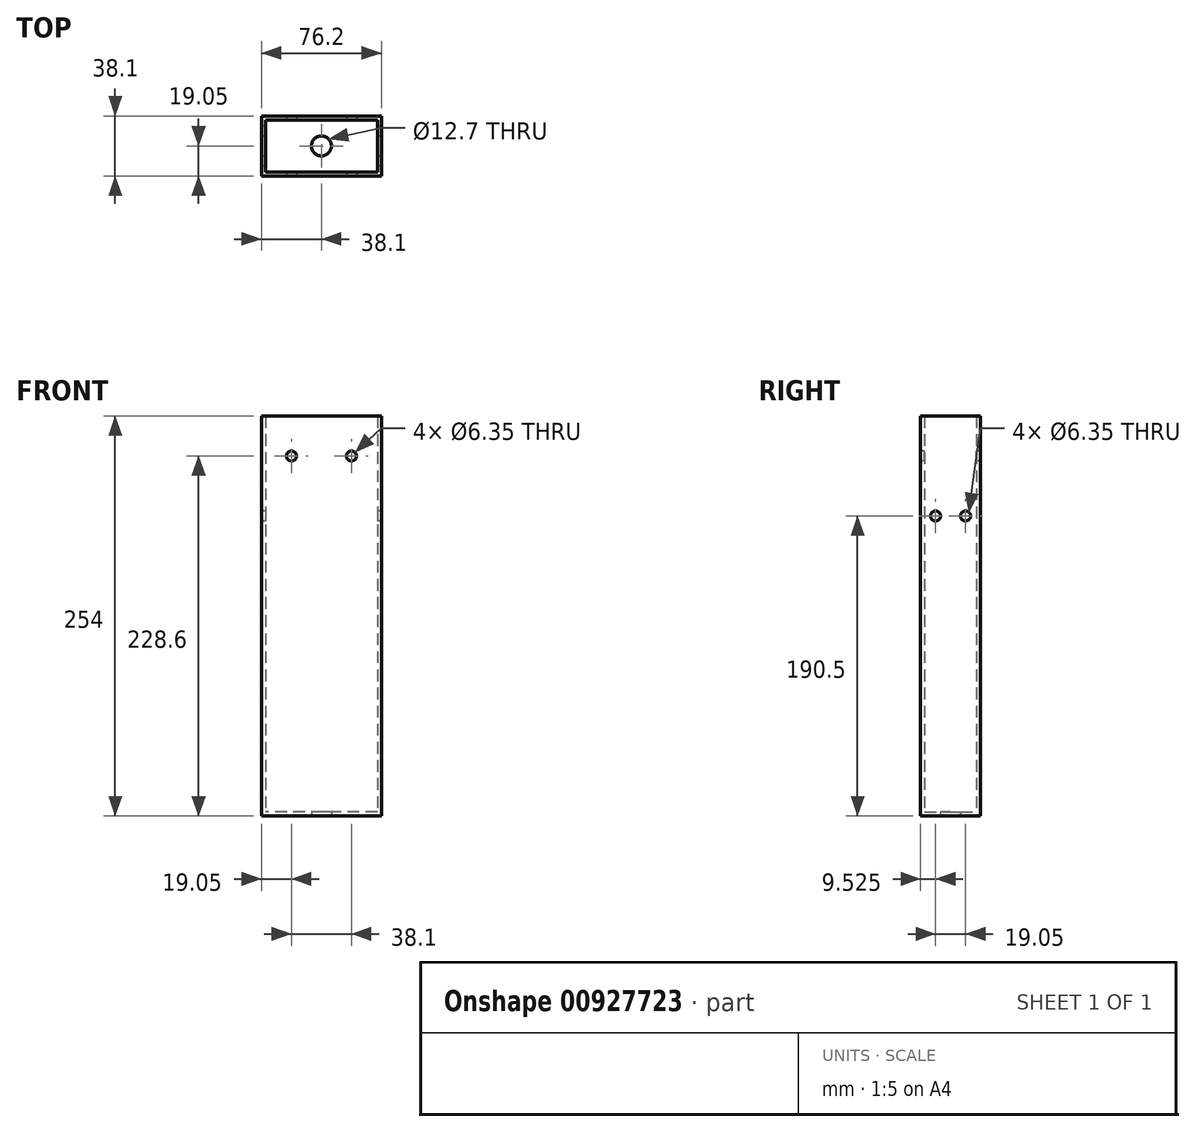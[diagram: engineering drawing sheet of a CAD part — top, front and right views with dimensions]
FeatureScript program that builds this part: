
annotation { "Feature Type Name" : "Feature", "Feature Type Description" : "" }
export const myFeature = defineFeature(function(context is Context, id is Id, definition is map)
    precondition{}
    {
        {
            var Q0;
            Q0=qCreatedBy(makeId("Top.planeOp"),FACE);
            var sketch = newSketch(context, id + "F0", { "sketchPlane" : qUnion([Q0])});
            skLineSegment(sketch, "E0.bottom", {"start": v(38.1, -19.05) * mm, "end": v(-38.1, -19.05) * mm});
            skLineSegment(sketch, "E0.top", {"start": v(38.1, 19.05) * mm, "end": v(-38.1, 19.05) * mm});
            skLineSegment(sketch, "E0.left", {"start": v(38.1, -19.05) * mm, "end": v(38.1, 19.05) * mm});
            skLineSegment(sketch, "E0.right", {"start": v(-38.1, -19.05) * mm, "end": v(-38.1, 19.05) * mm});
            skPoint(sketch, "E0.middle", {"position": v(0, 0) * mm});
            skSolve(sketch);
        }
        {
            var Q0;
            Q0=makeQuery(id+"F0.imprint","IMPRINT",FACE,{"disambiguationData":[TD([[makeQuery(id+"F0.imprint","IMPRINT",EDGE,{"derivedFrom":sQuery(id+"F0.wireOp",EDGE,"E0.bottom")}),-1.0]])]});
            extrude(context, id + "F1", {"entities" : qUnion([Q0]), "depth" : 254 * mm, "offsetDistance" : 25.4 * mm});
        }
        {
            var Q0;
            Q0=makeQuery(id+"F1.opExtrude","CAP_FACE",FACE,{"disambiguationData":[OSD([sQuery(id+"F0.wireOp",EDGE,"E0.bottom"),sQuery(id+"F0.wireOp",EDGE,"E0.top"),sQuery(id+"F0.wireOp",EDGE,"E0.left"),sQuery(id+"F0.wireOp",EDGE,"E0.right")])],"isStart":false});
            shell(context, id + "F2", {"entities" : qUnion([Q0]), "thickness" : 2.54 * mm});
        }
        {
            var Q0;
            Q0=makeQuery(id+"F1.opExtrude","SWEPT_FACE",FACE,{"disambiguationData":[OSD([sQuery(id+"F0.wireOp",EDGE,"E0.right")])]});
            var sketch = newSketch(context, id + "F3", { "sketchPlane" : qUnion([Q0])});
            skPoint(sketch, "E1", {"position": v(-9.52, 190.5) * mm});
            skPoint(sketch, "E2", {"position": v(9.53, 190.5) * mm});
            skSolve(sketch);
        }
        {
            var Q0;
            Q0=makeQuery(id+"F1.opExtrude","SWEPT_FACE",FACE,{"disambiguationData":[OSD([sQuery(id+"F0.wireOp",EDGE,"E0.bottom")])]});
            var sketch = newSketch(context, id + "F4", { "sketchPlane" : qUnion([Q0])});
            skPoint(sketch, "E3", {"position": v(-19.05, 228.6) * mm});
            skPoint(sketch, "E4", {"position": v(19.05, 228.6) * mm});
            skSolve(sketch);
        }
        {
            var Q0;
            Q0=sQuery(id+"F3.wireOp",VERTEX,"E1");
            var Q1;
            Q1=sQuery(id+"F3.wireOp",VERTEX,"E2");
            var Q2;
            Q2=sQuery(id+"F4.wireOp",VERTEX,"E3");
            var Q3;
            Q3=sQuery(id+"F4.wireOp",VERTEX,"E4");
            var Q4;
            Q4=makeQuery(id+"F1.opExtrude","SWEPT_BODY",BODY,{"disambiguationData":[OSD([sQuery(id+"F0.wireOp",EDGE,"E0.bottom"),sQuery(id+"F0.wireOp",EDGE,"E0.top"),sQuery(id+"F0.wireOp",EDGE,"E0.left"),sQuery(id+"F0.wireOp",EDGE,"E0.right")])]});
            hole(context, id + "F5", {"style" : HoleStyle.SIMPLE, "endStyle" : HoleEndStyle.THROUGH, "holeDiameter" : 6.35 * mm, "majorDiameter" : 6.35 * mm, "isTappedThrough" : true, "tappedDepth" : 12.7 * mm, "tapClearance" : 3, "locations" : qUnion([Q0, Q1, Q2, Q3]), "scope" : qUnion([Q4])});
        }
        {
            var Q0;
            Q0=makeQuery(id+"F1.opExtrude","CAP_FACE",FACE,{"disambiguationData":[OSD([sQuery(id+"F0.wireOp",EDGE,"E0.bottom"),sQuery(id+"F0.wireOp",EDGE,"E0.top"),sQuery(id+"F0.wireOp",EDGE,"E0.left"),sQuery(id+"F0.wireOp",EDGE,"E0.right")])],"isStart":true});
            var sketch = newSketch(context, id + "F6", { "sketchPlane" : qUnion([Q0])});
            skPoint(sketch, "E5", {"position": v(0, 0) * mm});
            skSolve(sketch);
        }
        {
            var Q0;
            Q0=sQuery(id+"F6.wireOp",VERTEX,"E5");
            var Q1;
            Q1=makeQuery(id+"F1.opExtrude","SWEPT_BODY",BODY,{"disambiguationData":[OSD([sQuery(id+"F0.wireOp",EDGE,"E0.bottom"),sQuery(id+"F0.wireOp",EDGE,"E0.top"),sQuery(id+"F0.wireOp",EDGE,"E0.left"),sQuery(id+"F0.wireOp",EDGE,"E0.right")])]});
            hole(context, id + "F7", {"style" : HoleStyle.SIMPLE, "endStyle" : HoleEndStyle.THROUGH, "holeDiameter" : 12.7 * mm, "majorDiameter" : 6.35 * mm, "isTappedThrough" : true, "tappedDepth" : 12.7 * mm, "tapClearance" : 3, "locations" : qUnion([Q0]), "scope" : qUnion([Q1])});
        }
    });
